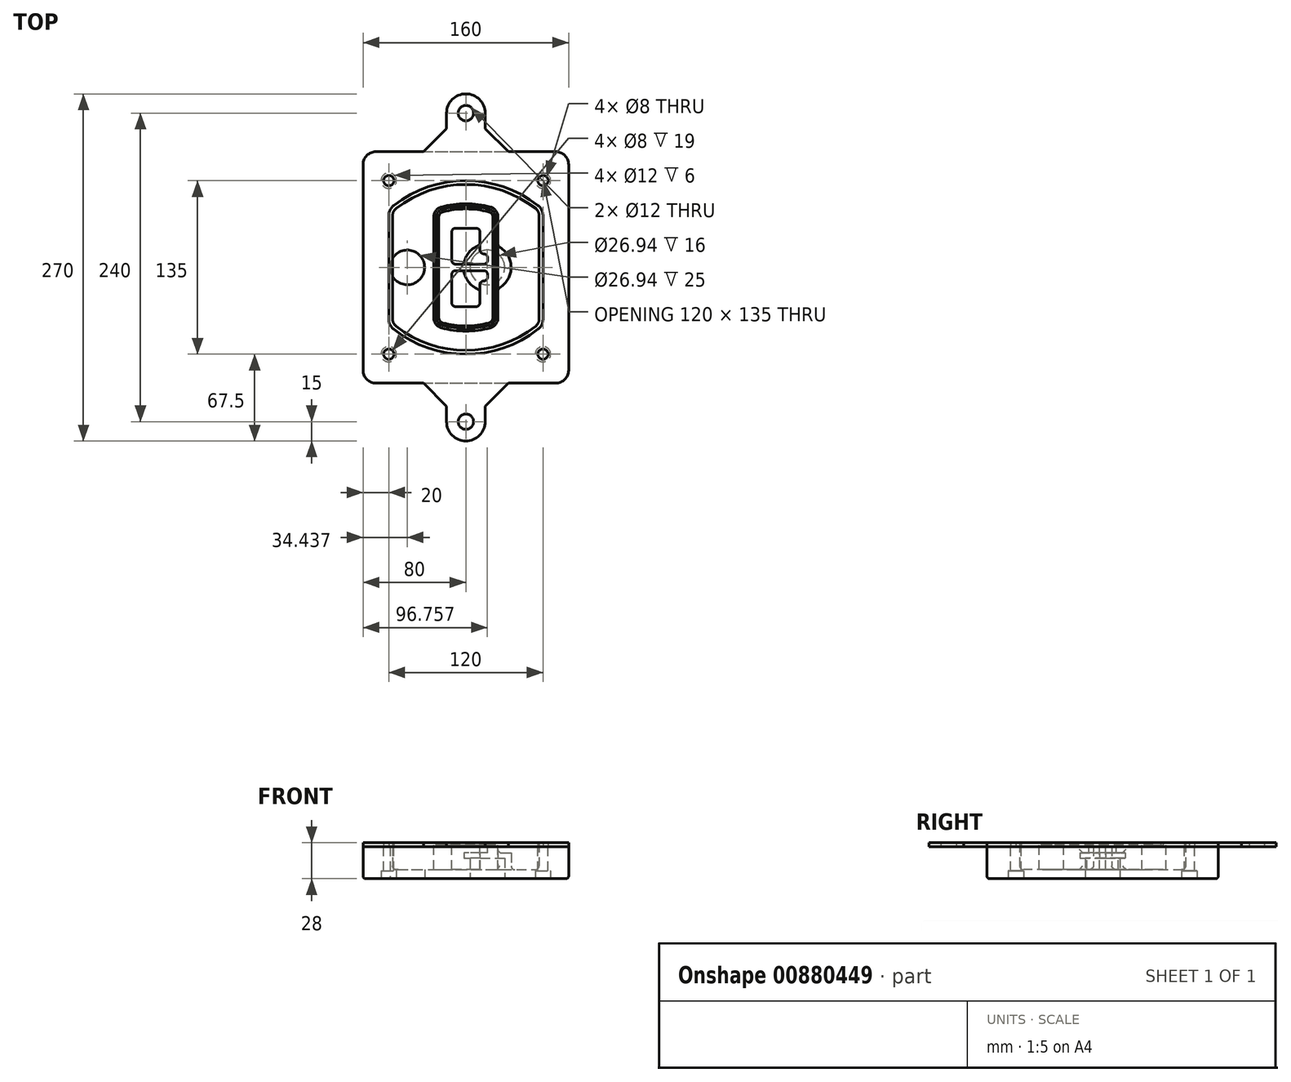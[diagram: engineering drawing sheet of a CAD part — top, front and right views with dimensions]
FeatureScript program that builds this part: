
annotation { "Feature Type Name" : "Feature", "Feature Type Description" : "" }
export const myFeature = defineFeature(function(context is Context, id is Id, definition is map)
    precondition{}
    {
        {
            var Q0;
            Q0=qCreatedBy(makeId("Top.planeOp"),FACE);
            var sketch = newSketch(context, id + "F0", { "sketchPlane" : qUnion([Q0])});
            skPoint(sketch, "E0.rect.middle", {"position": v(0, 0) * mm});
            skLineSegment(sketch, "E1.bottom", {"start": v(-70, -90) * mm, "end": v(70, -90) * mm});
            skLineSegment(sketch, "E1.top", {"start": v(-70, 90) * mm, "end": v(70, 90) * mm});
            skLineSegment(sketch, "E1.left", {"start": v(-80, -80) * mm, "end": v(-80, 80) * mm});
            skLineSegment(sketch, "E1.right", {"start": v(80, -80) * mm, "end": v(80, 80) * mm});
            skLineSegment(sketch, "E2", {"start": v(-80, 90) * mm, "end": v(80, -90) * mm, "construction": true});
            skLineSegment(sketch, "E3", {"start": v(80, 90) * mm, "end": v(-80, -90) * mm, "construction": true});
            skCircle(sketch, "E4", {"center": v(-60, 67.5) * mm, "radius": 4 * mm});
            skCircle(sketch, "E5", {"center": v(60, 67.5) * mm, "radius": 4 * mm});
            skCircle(sketch, "E6", {"center": v(60, -67.5) * mm, "radius": 4 * mm});
            skCircle(sketch, "E7", {"center": v(-60, -67.5) * mm, "radius": 4 * mm});
            skLineSegment(sketch, "E8", {"start": v(-60, 67.5) * mm, "end": v(60, 67.5) * mm, "construction": true});
            skLineSegment(sketch, "E9", {"start": v(60, 67.5) * mm, "end": v(60, -67.5) * mm, "construction": true});
            skLineSegment(sketch, "E10", {"start": v(60, -67.5) * mm, "end": v(-60, -67.5) * mm, "construction": true});
            skLineSegment(sketch, "E11", {"start": v(-60, -67.5) * mm, "end": v(-60, 67.5) * mm, "construction": true});
            skLineSegment(sketch, "E12", {"start": v(-60, 40.3) * mm, "end": v(-60, -40.3) * mm});
            skLineSegment(sketch, "E13", {"start": v(60, 40.3) * mm, "end": v(60, -40.3) * mm});
            skArc(sketch, "E14", {"start": v(56.15, 48.18) * mm, "mid": v(0, 67.5) * mm, "end": v(-56.15, 48.18) * mm});
            skArc(sketch, "E15", {"start": v(-56.15, -48.18) * mm, "mid": v(0, -67.5) * mm, "end": v(56.15, -48.18) * mm});
            skLineSegment(sketch, "E16", {"start": v(-60, 0) * mm, "end": v(60, 0) * mm, "construction": true});
            skPoint(sketch, "E17.visualSharp", {"position": v(-60, -45) * mm});
            skArc(sketch, "E17.filletArc", {"start": v(-60, -40.3) * mm, "mid": v(-58.99, -44.68) * mm, "end": v(-56.15, -48.18) * mm});
            skPoint(sketch, "E18.visualSharp", {"position": v(-60, 45) * mm});
            skArc(sketch, "E18.filletArc", {"start": v(-56.15, 48.18) * mm, "mid": v(-58.99, 44.68) * mm, "end": v(-60, 40.3) * mm});
            skPoint(sketch, "E19.visualSharp", {"position": v(60, 45) * mm});
            skArc(sketch, "E19.filletArc", {"start": v(60, 40.3) * mm, "mid": v(58.99, 44.68) * mm, "end": v(56.15, 48.18) * mm});
            skPoint(sketch, "E20.visualSharp", {"position": v(60, -45) * mm});
            skArc(sketch, "E20.filletArc", {"start": v(56.15, -48.18) * mm, "mid": v(58.99, -44.68) * mm, "end": v(60, -40.3) * mm});
            skPoint(sketch, "E21.visualSharp", {"position": v(-80, 90) * mm});
            skArc(sketch, "E21.filletArc", {"start": v(-70, 90) * mm, "mid": v(-77.07, 87.07) * mm, "end": v(-80, 80) * mm});
            skPoint(sketch, "E22.visualSharp", {"position": v(80, 90) * mm});
            skArc(sketch, "E22.filletArc", {"start": v(80, 80) * mm, "mid": v(77.07, 87.07) * mm, "end": v(70, 90) * mm});
            skPoint(sketch, "E23.visualSharp", {"position": v(80, -90) * mm});
            skArc(sketch, "E23.filletArc", {"start": v(70, -90) * mm, "mid": v(77.07, -87.07) * mm, "end": v(80, -80) * mm});
            skPoint(sketch, "E24.visualSharp", {"position": v(-80, -90) * mm});
            skArc(sketch, "E24.filletArc", {"start": v(-80, -80) * mm, "mid": v(-77.07, -87.07) * mm, "end": v(-70, -90) * mm});
            skArc(sketch, "E25.0", {"start": v(57, 40.3) * mm, "mid": v(56.3, 43.36) * mm, "end": v(54.3, 45.81) * mm});
            skLineSegment(sketch, "E25.1", {"start": v(57, 40.3) * mm, "end": v(57, -40.3) * mm});
            skArc(sketch, "E25.2", {"start": v(54.3, -45.81) * mm, "mid": v(56.3, -43.36) * mm, "end": v(57, -40.3) * mm});
            skArc(sketch, "E25.3", {"start": v(-54.3, -45.81) * mm, "mid": v(0, -64.5) * mm, "end": v(54.3, -45.81) * mm});
            skArc(sketch, "E25.4", {"start": v(-57, -40.3) * mm, "mid": v(-56.3, -43.36) * mm, "end": v(-54.3, -45.81) * mm});
            skArc(sketch, "E25.5", {"start": v(54.3, 45.81) * mm, "mid": v(0, 64.5) * mm, "end": v(-54.3, 45.81) * mm});
            skLineSegment(sketch, "E25.6", {"start": v(-57, 40.3) * mm, "end": v(-57, -40.3) * mm});
            skArc(sketch, "E25.7", {"start": v(-54.3, 45.81) * mm, "mid": v(-56.3, 43.36) * mm, "end": v(-57, 40.3) * mm});
            skArc(sketch, "E26.0", {"start": v(-58.62, 51.33) * mm, "mid": v(-62.58, 46.43) * mm, "end": v(-64, 40.3) * mm});
            skArc(sketch, "E26.1", {"start": v(58.62, 51.33) * mm, "mid": v(0, 71.5) * mm, "end": v(-58.62, 51.33) * mm});
            skArc(sketch, "E26.2", {"start": v(64, 40.3) * mm, "mid": v(62.58, 46.43) * mm, "end": v(58.62, 51.33) * mm});
            skLineSegment(sketch, "E26.3", {"start": v(64, 40.3) * mm, "end": v(64, -40.3) * mm});
            skArc(sketch, "E26.4", {"start": v(58.62, -51.33) * mm, "mid": v(62.58, -46.43) * mm, "end": v(64, -40.3) * mm});
            skLineSegment(sketch, "E26.5", {"start": v(-64, 40.3) * mm, "end": v(-64, -40.3) * mm});
            skArc(sketch, "E26.6", {"start": v(-58.62, -51.33) * mm, "mid": v(0, -71.5) * mm, "end": v(58.62, -51.33) * mm});
            skArc(sketch, "E26.7", {"start": v(-64, -40.3) * mm, "mid": v(-62.58, -46.43) * mm, "end": v(-58.62, -51.33) * mm});
            skSolve(sketch);
        }
        {
            var Q0;
            Q0=makeQuery(id+"F0.imprint","IMPRINT",FACE,{"disambiguationData":[TD([[makeQuery(id+"F0.imprint","IMPRINT",EDGE,{"derivedFrom":sQuery(id+"F0.wireOp",EDGE,"E1.bottom")}),1.0]])]});
            var Q1;
            Q1=makeQuery(id+"F0.imprint","IMPRINT",FACE,{"disambiguationData":[TD([[makeQuery(id+"F0.imprint","IMPRINT",EDGE,{"derivedFrom":sQuery(id+"F0.wireOp",EDGE,"E12")}),1.0]])]});
            var Q2;
            Q2=makeQuery(id+"F0.imprint","IMPRINT",FACE,{"disambiguationData":[TD([[makeQuery(id+"F0.imprint","IMPRINT",EDGE,{"derivedFrom":sQuery(id+"F0.wireOp",EDGE,"E25.0")}),1.0]])]});
            var Q3;
            Q3=makeQuery(id+"F0.imprint","IMPRINT",FACE,{"disambiguationData":[TD([[makeQuery(id+"F0.imprint","IMPRINT",EDGE,{"derivedFrom":sQuery(id+"F0.wireOp",EDGE,"E12")}),-1.0]])]});
            extrude(context, id + "F1", {"entities" : qUnion([Q0, Q1, Q2, Q3]), "oppositeDirection" : true, "depth" : 25 * mm});
        }
        {
            var Q0;
            Q0=makeQuery(id+"F0.imprint","IMPRINT",FACE,{"disambiguationData":[TD([[makeQuery(id+"F0.imprint","IMPRINT",EDGE,{"derivedFrom":sQuery(id+"F0.wireOp",EDGE,"E12")}),1.0]])]});
            extrude(context, id + "F2", {"entities" : qUnion([Q0]), "operationType" : NewBodyOperationType.ADD, "depth" : 3 * mm});
        }
        {
            var Q0;
            Q0=makeQuery(id+"F0.imprint","IMPRINT",FACE,{"disambiguationData":[TD([[makeQuery(id+"F0.imprint","IMPRINT",EDGE,{"derivedFrom":sQuery(id+"F0.wireOp",EDGE,"E25.0")}),1.0]])]});
            extrude(context, id + "F3", {"entities" : qUnion([Q0]), "operationType" : NewBodyOperationType.REMOVE, "oppositeDirection" : true, "depth" : 18 * mm});
        }
        {
            var Q0;
            Q0=makeQuery(id+"F2.opExtrude","CAP_FACE",FACE,{"disambiguationData":[OSD([sQuery(id+"F0.wireOp",EDGE,"E12"),sQuery(id+"F0.wireOp",EDGE,"E13"),sQuery(id+"F0.wireOp",EDGE,"E14"),sQuery(id+"F0.wireOp",EDGE,"E15"),sQuery(id+"F0.wireOp",EDGE,"E17.filletArc"),sQuery(id+"F0.wireOp",EDGE,"E18.filletArc"),sQuery(id+"F0.wireOp",EDGE,"E19.filletArc"),sQuery(id+"F0.wireOp",EDGE,"E20.filletArc"),sQuery(id+"F0.wireOp",EDGE,"E25.0"),sQuery(id+"F0.wireOp",EDGE,"E25.1"),sQuery(id+"F0.wireOp",EDGE,"E25.2"),sQuery(id+"F0.wireOp",EDGE,"E25.3"),sQuery(id+"F0.wireOp",EDGE,"E25.4"),sQuery(id+"F0.wireOp",EDGE,"E25.5"),sQuery(id+"F0.wireOp",EDGE,"E25.6"),sQuery(id+"F0.wireOp",EDGE,"E25.7")])],"isStart":false});
            var sketch = newSketch(context, id + "F4", { "sketchPlane" : qUnion([Q0])});
            skArc(sketch, "E27.0", {"start": v(-19.08, -46.97) * mm, "mid": v(0, -49.5) * mm, "end": v(19.08, -46.97) * mm});
            skArc(sketch, "E28.0", {"start": v(19.08, 46.97) * mm, "mid": v(0, 49.5) * mm, "end": v(-19.08, 46.97) * mm});
            skLineSegment(sketch, "E29", {"start": v(-25, 39.25) * mm, "end": v(-25, -39.25) * mm});
            skLineSegment(sketch, "E30", {"start": v(25, 39.25) * mm, "end": v(25, -39.25) * mm});
            skLineSegment(sketch, "E31", {"start": v(-25, 45.1) * mm, "end": v(25, 45.1) * mm, "construction": true});
            skLineSegment(sketch, "E32", {"start": v(-25, -45.1) * mm, "end": v(25, -45.1) * mm, "construction": true});
            skPoint(sketch, "E33.visualSharp", {"position": v(-25, 45.1) * mm});
            skArc(sketch, "E33.filletArc", {"start": v(-19.08, 46.97) * mm, "mid": v(-23.35, 44.11) * mm, "end": v(-25, 39.25) * mm});
            skPoint(sketch, "E34.visualSharp", {"position": v(25, 45.1) * mm});
            skArc(sketch, "E34.filletArc", {"start": v(25, 39.25) * mm, "mid": v(23.35, 44.11) * mm, "end": v(19.08, 46.97) * mm});
            skPoint(sketch, "E35.visualSharp", {"position": v(25, -45.1) * mm});
            skArc(sketch, "E35.filletArc", {"start": v(19.08, -46.97) * mm, "mid": v(23.35, -44.11) * mm, "end": v(25, -39.25) * mm});
            skPoint(sketch, "E36.visualSharp", {"position": v(-25, -45.1) * mm});
            skArc(sketch, "E36.filletArc", {"start": v(-25, -39.25) * mm, "mid": v(-23.35, -44.11) * mm, "end": v(-19.08, -46.97) * mm});
            skArc(sketch, "E37.0", {"start": v(54.3, 45.81) * mm, "mid": v(0, 64.5) * mm, "end": v(-54.3, 45.81) * mm});
            skArc(sketch, "E37.1", {"start": v(-54.3, 45.81) * mm, "mid": v(-56.3, 43.36) * mm, "end": v(-57, 40.3) * mm});
            skLineSegment(sketch, "E37.2", {"start": v(-57, 40.3) * mm, "end": v(-57, -40.3) * mm});
            skArc(sketch, "E37.3", {"start": v(-57, -40.3) * mm, "mid": v(-56.3, -43.36) * mm, "end": v(-54.3, -45.81) * mm});
            skArc(sketch, "E37.4", {"start": v(-54.3, -45.81) * mm, "mid": v(0, -64.5) * mm, "end": v(54.3, -45.81) * mm});
            skArc(sketch, "E37.5", {"start": v(54.3, -45.81) * mm, "mid": v(56.3, -43.36) * mm, "end": v(57, -40.3) * mm});
            skLineSegment(sketch, "E37.6", {"start": v(57, 40.3) * mm, "end": v(57, -40.3) * mm});
            skArc(sketch, "E37.7", {"start": v(57, 40.3) * mm, "mid": v(56.3, 43.36) * mm, "end": v(54.3, 45.81) * mm});
            skLineSegment(sketch, "E38.0", {"start": v(23, 39.25) * mm, "end": v(23, -39.25) * mm});
            skArc(sketch, "E38.1", {"start": v(18.56, -45.04) * mm, "mid": v(21.76, -42.9) * mm, "end": v(23, -39.25) * mm});
            skArc(sketch, "E38.2", {"start": v(-18.56, -45.04) * mm, "mid": v(0, -47.5) * mm, "end": v(18.56, -45.04) * mm});
            skArc(sketch, "E38.3", {"start": v(-23, -39.25) * mm, "mid": v(-21.76, -42.9) * mm, "end": v(-18.56, -45.04) * mm});
            skLineSegment(sketch, "E38.4", {"start": v(-23, 39.25) * mm, "end": v(-23, -39.25) * mm});
            skArc(sketch, "E38.5", {"start": v(23, 39.25) * mm, "mid": v(21.76, 42.9) * mm, "end": v(18.56, 45.04) * mm});
            skArc(sketch, "E38.6", {"start": v(-18.56, 45.04) * mm, "mid": v(-21.76, 42.9) * mm, "end": v(-23, 39.25) * mm});
            skArc(sketch, "E38.7", {"start": v(18.56, 45.04) * mm, "mid": v(0, 47.5) * mm, "end": v(-18.56, 45.04) * mm});
            skArc(sketch, "E39.0", {"start": v(21, 39.25) * mm, "mid": v(20.18, 41.68) * mm, "end": v(18.04, 43.1) * mm});
            skLineSegment(sketch, "E39.1", {"start": v(21, 39.25) * mm, "end": v(21, -39.25) * mm});
            skArc(sketch, "E39.2", {"start": v(18.04, -43.1) * mm, "mid": v(20.18, -41.68) * mm, "end": v(21, -39.25) * mm});
            skArc(sketch, "E39.3", {"start": v(-18.04, -43.1) * mm, "mid": v(0, -45.5) * mm, "end": v(18.04, -43.1) * mm});
            skArc(sketch, "E39.4", {"start": v(-21, -39.25) * mm, "mid": v(-20.18, -41.68) * mm, "end": v(-18.04, -43.1) * mm});
            skArc(sketch, "E39.5", {"start": v(18.04, 43.1) * mm, "mid": v(0, 45.5) * mm, "end": v(-18.04, 43.1) * mm});
            skLineSegment(sketch, "E39.6", {"start": v(-21, 39.25) * mm, "end": v(-21, -39.25) * mm});
            skArc(sketch, "E39.7", {"start": v(-18.04, 43.1) * mm, "mid": v(-20.18, 41.68) * mm, "end": v(-21, 39.25) * mm});
            skLineSegment(sketch, "E40", {"start": v(-25, 0) * mm, "end": v(25, 0) * mm, "construction": true});
            skLineSegment(sketch, "E41", {"start": v(-11, 5.5) * mm, "end": v(-11, 27.5) * mm});
            skLineSegment(sketch, "E42", {"start": v(-8, 30.5) * mm, "end": v(8, 30.5) * mm});
            skLineSegment(sketch, "E43", {"start": v(11, 27.5) * mm, "end": v(11, 13.5) * mm});
            skLineSegment(sketch, "E44", {"start": v(14, 10.5) * mm, "end": v(14, 10.5) * mm});
            skLineSegment(sketch, "E45", {"start": v(17, 7.5) * mm, "end": v(17, 5.5) * mm});
            skLineSegment(sketch, "E46", {"start": v(14, 2.5) * mm, "end": v(-8, 2.5) * mm});
            skPoint(sketch, "E47.visualSharp", {"position": v(-11, 30.5) * mm});
            skArc(sketch, "E47.filletArc", {"start": v(-8, 30.5) * mm, "mid": v(-10.12, 29.62) * mm, "end": v(-11, 27.5) * mm});
            skPoint(sketch, "E48.visualSharp", {"position": v(11, 30.5) * mm});
            skArc(sketch, "E48.filletArc", {"start": v(11, 27.5) * mm, "mid": v(10.12, 29.62) * mm, "end": v(8, 30.5) * mm});
            skPoint(sketch, "E49.visualSharp", {"position": v(11, 10.5) * mm});
            skArc(sketch, "E49.filletArc", {"start": v(11, 13.5) * mm, "mid": v(11.88, 11.38) * mm, "end": v(14, 10.5) * mm});
            skPoint(sketch, "E50.visualSharp", {"position": v(17, 10.5) * mm});
            skArc(sketch, "E50.filletArc", {"start": v(17, 7.5) * mm, "mid": v(16.12, 9.62) * mm, "end": v(14, 10.5) * mm});
            skPoint(sketch, "E51.visualSharp", {"position": v(17, 2.5) * mm});
            skArc(sketch, "E51.filletArc", {"start": v(14, 2.5) * mm, "mid": v(16.12, 3.38) * mm, "end": v(17, 5.5) * mm});
            skPoint(sketch, "E52.visualSharp", {"position": v(-11, 2.5) * mm});
            skArc(sketch, "E52.filletArc", {"start": v(-11, 5.5) * mm, "mid": v(-10.12, 3.38) * mm, "end": v(-8, 2.5) * mm});
            skLineSegment(sketch, "E53.0.MirrorCS", {"start": v(14, -2.5) * mm, "end": v(-8, -2.5) * mm});
            skArc(sketch, "E54.0.MirrorCS", {"start": v(-11, -5.5) * mm, "mid": v(-10.12, -3.38) * mm, "end": v(-8, -2.5) * mm});
            skLineSegment(sketch, "E55.0.MirrorCS", {"start": v(-11, -5.5) * mm, "end": v(-11, -27.5) * mm});
            skArc(sketch, "E56.0.MirrorCS", {"start": v(-8, -30.5) * mm, "mid": v(-10.12, -29.62) * mm, "end": v(-11, -27.5) * mm});
            skLineSegment(sketch, "E57.0.MirrorCS", {"start": v(-8, -30.5) * mm, "end": v(8, -30.5) * mm});
            skArc(sketch, "E58.0.MirrorCS", {"start": v(11, -27.5) * mm, "mid": v(10.12, -29.62) * mm, "end": v(8, -30.5) * mm});
            skLineSegment(sketch, "E59.0.MirrorCS", {"start": v(11, -27.5) * mm, "end": v(11, -13.5) * mm});
            skArc(sketch, "E60.0.MirrorCS", {"start": v(11, -13.5) * mm, "mid": v(11.88, -11.38) * mm, "end": v(14, -10.5) * mm});
            skArc(sketch, "E61.0.MirrorCS", {"start": v(17, -7.5) * mm, "mid": v(16.12, -9.62) * mm, "end": v(14, -10.5) * mm});
            skLineSegment(sketch, "E62.0.MirrorCS", {"start": v(17, -7.5) * mm, "end": v(17, -5.5) * mm});
            skArc(sketch, "E63.0.MirrorCS", {"start": v(14, -2.5) * mm, "mid": v(16.12, -3.38) * mm, "end": v(17, -5.5) * mm});
            skSolve(sketch);
        }
        {
            var Q0;
            Q0=makeQuery(id+"F4.imprint","IMPRINT",FACE,{"disambiguationData":[TD([[makeQuery(id+"F4.imprint","IMPRINT",EDGE,{"derivedFrom":sQuery(id+"F4.wireOp",EDGE,"E27.0")}),1.0]])]});
            var Q1;
            Q1=makeQuery(id+"F4.imprint","IMPRINT",FACE,{"disambiguationData":[TD([[makeQuery(id+"F4.imprint","IMPRINT",EDGE,{"derivedFrom":sQuery(id+"F4.wireOp",EDGE,"E38.0")}),-1.0]])]});
            var Q2;
            Q2=makeQuery(id+"F4.imprint","IMPRINT",FACE,{"disambiguationData":[TD([[makeQuery(id+"F4.imprint","IMPRINT",EDGE,{"derivedFrom":sQuery(id+"F4.wireOp",EDGE,"E39.0")}),1.0]])]});
            extrude(context, id + "F5", {"entities" : qUnion([Q0, Q1, Q2]), "operationType" : NewBodyOperationType.ADD, "endBound" : BoundingType.UP_TO_NEXT, "oppositeDirection" : true, "depth" : 25 * mm});
        }
        {
            var Q0;
            Q0=makeQuery(id+"F4.imprint","IMPRINT",FACE,{"disambiguationData":[TD([[makeQuery(id+"F4.imprint","IMPRINT",EDGE,{"derivedFrom":sQuery(id+"F4.wireOp",EDGE,"E38.0")}),-1.0]])]});
            extrude(context, id + "F6", {"entities" : qUnion([Q0]), "operationType" : NewBodyOperationType.REMOVE, "oppositeDirection" : true, "depth" : 2 * mm});
        }
        {
            var Q0;
            Q0=makeQuery(id+"F1.opExtrude","CAP_FACE",FACE,{"disambiguationData":[OSD([sQuery(id+"F0.wireOp",EDGE,"E1.bottom"),sQuery(id+"F0.wireOp",EDGE,"E1.top"),sQuery(id+"F0.wireOp",EDGE,"E1.left"),sQuery(id+"F0.wireOp",EDGE,"E1.right"),sQuery(id+"F0.wireOp",EDGE,"E4"),sQuery(id+"F0.wireOp",EDGE,"E5"),sQuery(id+"F0.wireOp",EDGE,"E6"),sQuery(id+"F0.wireOp",EDGE,"E7"),sQuery(id+"F0.wireOp",EDGE,"E21.filletArc"),sQuery(id+"F0.wireOp",EDGE,"E22.filletArc"),sQuery(id+"F0.wireOp",EDGE,"E23.filletArc"),sQuery(id+"F0.wireOp",EDGE,"E24.filletArc")])],"isStart":false});
            var sketch = newSketch(context, id + "F7", { "sketchPlane" : qUnion([Q0])});
            skCircle(sketch, "E64", {"center": v(16.76, 0) * mm, "radius": 13.47 * mm});
            skCircle(sketch, "E65", {"center": v(-45.56, 0) * mm, "radius": 13.47 * mm});
            skLineSegment(sketch, "E66", {"start": v(80, 0) * mm, "end": v(-80, 0) * mm});
            skCircle(sketch, "E67", {"center": v(16.76, 0) * mm, "radius": 18.47 * mm});
            skCircle(sketch, "E68", {"center": v(60, -67.5) * mm, "radius": 6 * mm});
            skCircle(sketch, "E69", {"center": v(-60, -67.5) * mm, "radius": 6 * mm});
            skCircle(sketch, "E70", {"center": v(-60, 67.5) * mm, "radius": 6 * mm});
            skCircle(sketch, "E71", {"center": v(60, 67.5) * mm, "radius": 6 * mm});
            skSolve(sketch);
        }
        {
            var Q0;
            {var subQ1=sQuery(id+"F7.wireOp",EDGE,"E66");var subQ4=sQuery(id+"F7.wireOp",EDGE,"E64");var subQ6=makeQuery(id+"F7.imprint","INTERSECT",VERTEX,{"disambiguationData":[OD(0.0)],"derivedFrom":[subQ4,subQ1]});Q0=makeQuery(id+"F7.imprint","IMPRINT",FACE,{"disambiguationData":[TD([[makeQuery(id+"F7.imprint","IMPRINT",EDGE,{"disambiguationData":[TD([[subQ6,-1.0]])],"derivedFrom":subQ4}),-1.0]])]});}
            var Q1;
            {var subQ0=sQuery(id+"F7.wireOp",EDGE,"E66");var subQ1=sQuery(id+"F7.wireOp",EDGE,"E64");var subQ3=makeQuery(id+"F7.imprint","INTERSECT",VERTEX,{"disambiguationData":[OD(0.0)],"derivedFrom":[subQ1,subQ0]});Q1=makeQuery(id+"F7.imprint","IMPRINT",FACE,{"disambiguationData":[TD([[makeQuery(id+"F7.imprint","IMPRINT",EDGE,{"disambiguationData":[TD([[subQ3,-1.0]])],"derivedFrom":subQ1}),1.0]])]});}
            var Q2;
            {var subQ0=sQuery(id+"F7.wireOp",EDGE,"E66");var subQ1=sQuery(id+"F7.wireOp",EDGE,"E64");var subQ3=makeQuery(id+"F7.imprint","INTERSECT",VERTEX,{"disambiguationData":[OD(0.0)],"derivedFrom":[subQ1,subQ0]});Q2=makeQuery(id+"F7.imprint","IMPRINT",FACE,{"disambiguationData":[TD([[makeQuery(id+"F7.imprint","IMPRINT",EDGE,{"disambiguationData":[TD([[subQ3,1.0]])],"derivedFrom":subQ1}),1.0]])]});}
            var Q3;
            {var subQ1=sQuery(id+"F7.wireOp",EDGE,"E66");var subQ4=sQuery(id+"F7.wireOp",EDGE,"E64");var subQ6=makeQuery(id+"F7.imprint","INTERSECT",VERTEX,{"disambiguationData":[OD(0.0)],"derivedFrom":[subQ4,subQ1]});Q3=makeQuery(id+"F7.imprint","IMPRINT",FACE,{"disambiguationData":[TD([[makeQuery(id+"F7.imprint","IMPRINT",EDGE,{"disambiguationData":[TD([[subQ6,1.0]])],"derivedFrom":subQ4}),-1.0]])]});}
            extrude(context, id + "F8", {"entities" : qUnion([Q0, Q1, Q2, Q3]), "operationType" : NewBodyOperationType.ADD, "oppositeDirection" : true, "depth" : 20 * mm});
        }
        {
            var Q0;
            {var subQ0=sQuery(id+"F7.wireOp",EDGE,"E66");var subQ1=sQuery(id+"F7.wireOp",EDGE,"E64");var subQ3=makeQuery(id+"F7.imprint","INTERSECT",VERTEX,{"disambiguationData":[OD(0.0)],"derivedFrom":[subQ1,subQ0]});Q0=makeQuery(id+"F7.imprint","IMPRINT",FACE,{"disambiguationData":[TD([[makeQuery(id+"F7.imprint","IMPRINT",EDGE,{"disambiguationData":[TD([[subQ3,-1.0]])],"derivedFrom":subQ1}),1.0]])]});}
            var Q1;
            {var subQ0=sQuery(id+"F7.wireOp",EDGE,"E66");var subQ1=sQuery(id+"F7.wireOp",EDGE,"E64");var subQ3=makeQuery(id+"F7.imprint","INTERSECT",VERTEX,{"disambiguationData":[OD(0.0)],"derivedFrom":[subQ1,subQ0]});Q1=makeQuery(id+"F7.imprint","IMPRINT",FACE,{"disambiguationData":[TD([[makeQuery(id+"F7.imprint","IMPRINT",EDGE,{"disambiguationData":[TD([[subQ3,1.0]])],"derivedFrom":subQ1}),1.0]])]});}
            extrude(context, id + "F9", {"entities" : qUnion([Q0, Q1]), "operationType" : NewBodyOperationType.REMOVE, "oppositeDirection" : true, "depth" : 16 * mm});
        }
        {
            var Q0;
            {var subQ0=sQuery(id+"F7.wireOp",EDGE,"E66");var subQ1=sQuery(id+"F7.wireOp",EDGE,"E65");var subQ3=makeQuery(id+"F7.imprint","INTERSECT",VERTEX,{"disambiguationData":[OD(0.0)],"derivedFrom":[subQ1,subQ0]});Q0=makeQuery(id+"F7.imprint","IMPRINT",FACE,{"disambiguationData":[TD([[makeQuery(id+"F7.imprint","IMPRINT",EDGE,{"disambiguationData":[TD([[subQ3,-1.0]])],"derivedFrom":subQ1}),1.0]])]});}
            var Q1;
            {var subQ0=sQuery(id+"F7.wireOp",EDGE,"E66");var subQ1=sQuery(id+"F7.wireOp",EDGE,"E65");var subQ3=makeQuery(id+"F7.imprint","INTERSECT",VERTEX,{"disambiguationData":[OD(0.0)],"derivedFrom":[subQ1,subQ0]});Q1=makeQuery(id+"F7.imprint","IMPRINT",FACE,{"disambiguationData":[TD([[makeQuery(id+"F7.imprint","IMPRINT",EDGE,{"disambiguationData":[TD([[subQ3,1.0]])],"derivedFrom":subQ1}),1.0]])]});}
            extrude(context, id + "F10", {"entities" : qUnion([Q0, Q1]), "operationType" : NewBodyOperationType.REMOVE, "oppositeDirection" : true, "depth" : 25 * mm});
        }
        {
            var Q0;
            Q0=makeQuery(id+"F7.imprint","IMPRINT",FACE,{"disambiguationData":[TD([[makeQuery(id+"F7.imprint","IMPRINT",EDGE,{"derivedFrom":sQuery(id+"F7.wireOp",EDGE,"E68")}),1.0]])]});
            var Q1;
            Q1=makeQuery(id+"F7.imprint","IMPRINT",FACE,{"disambiguationData":[TD([[makeQuery(id+"F7.imprint","IMPRINT",EDGE,{"derivedFrom":makeQuery(id+"F1.opExtrude","CAP_EDGE",EDGE,{"disambiguationData":[OSD([sQuery(id+"F0.wireOp",EDGE,"E5")])],"isStart":false})}),-1.0]])]});
            var Q2;
            Q2=makeQuery(id+"F7.imprint","IMPRINT",FACE,{"disambiguationData":[TD([[makeQuery(id+"F7.imprint","IMPRINT",EDGE,{"derivedFrom":sQuery(id+"F7.wireOp",EDGE,"E69")}),1.0]])]});
            var Q3;
            Q3=makeQuery(id+"F7.imprint","IMPRINT",FACE,{"disambiguationData":[TD([[makeQuery(id+"F7.imprint","IMPRINT",EDGE,{"derivedFrom":makeQuery(id+"F1.opExtrude","CAP_EDGE",EDGE,{"disambiguationData":[OSD([sQuery(id+"F0.wireOp",EDGE,"E4")])],"isStart":false})}),-1.0]])]});
            var Q4;
            Q4=makeQuery(id+"F7.imprint","IMPRINT",FACE,{"disambiguationData":[TD([[makeQuery(id+"F7.imprint","IMPRINT",EDGE,{"derivedFrom":sQuery(id+"F7.wireOp",EDGE,"E70")}),1.0]])]});
            var Q5;
            Q5=makeQuery(id+"F7.imprint","IMPRINT",FACE,{"disambiguationData":[TD([[makeQuery(id+"F7.imprint","IMPRINT",EDGE,{"derivedFrom":makeQuery(id+"F1.opExtrude","CAP_EDGE",EDGE,{"disambiguationData":[OSD([sQuery(id+"F0.wireOp",EDGE,"E7")])],"isStart":false})}),-1.0]])]});
            var Q6;
            Q6=makeQuery(id+"F7.imprint","IMPRINT",FACE,{"disambiguationData":[TD([[makeQuery(id+"F7.imprint","IMPRINT",EDGE,{"derivedFrom":sQuery(id+"F7.wireOp",EDGE,"E71")}),1.0]])]});
            var Q7;
            Q7=makeQuery(id+"F7.imprint","IMPRINT",FACE,{"disambiguationData":[TD([[makeQuery(id+"F7.imprint","IMPRINT",EDGE,{"derivedFrom":makeQuery(id+"F1.opExtrude","CAP_EDGE",EDGE,{"disambiguationData":[OSD([sQuery(id+"F0.wireOp",EDGE,"E6")])],"isStart":false})}),-1.0]])]});
            extrude(context, id + "F11", {"entities" : qUnion([Q0, Q1, Q2, Q3, Q4, Q5, Q6, Q7]), "operationType" : NewBodyOperationType.REMOVE, "oppositeDirection" : true, "depth" : 6 * mm});
        }
        {
            var Q0;
            Q0=makeQuery(id+"F9.boolean.opBoolean","COPY",FACE,{"derivedFrom":makeQuery(id+"F9.opExtrude","CAP_FACE",FACE,{"disambiguationData":[OSD([sQuery(id+"F7.wireOp",EDGE,"E64")])],"isStart":false})});
            var sketch = newSketch(context, id + "F12", { "sketchPlane" : qUnion([Q0])});
            skArc(sketch, "E72.0", {"start": v(11, 17.55) * mm, "mid": v(2.57, 11.82) * mm, "end": v(-1.54, 2.5) * mm});
            skArc(sketch, "E72.1", {"start": v(-1.54, -2.5) * mm, "mid": v(2.57, -11.82) * mm, "end": v(11, -17.55) * mm});
            skLineSegment(sketch, "E73", {"start": v(-1.54, -2.5) * mm, "end": v(14, -2.5) * mm});
            skLineSegment(sketch, "E74.0", {"start": v(14, 2.5) * mm, "end": v(-1.54, 2.5) * mm});
            skArc(sketch, "E74.1", {"start": v(14, 2.5) * mm, "mid": v(16.12, 3.38) * mm, "end": v(17, 5.5) * mm});
            skLineSegment(sketch, "E74.2", {"start": v(17, 7.5) * mm, "end": v(17, 5.5) * mm});
            skArc(sketch, "E74.3", {"start": v(17, 7.5) * mm, "mid": v(16.12, 9.62) * mm, "end": v(14, 10.5) * mm});
            skArc(sketch, "E74.4", {"start": v(11, 13.5) * mm, "mid": v(11.88, 11.38) * mm, "end": v(14, 10.5) * mm});
            skLineSegment(sketch, "E74.5", {"start": v(11, 17.55) * mm, "end": v(11, 13.5) * mm});
            skLineSegment(sketch, "E74.7", {"start": v(14, -2.5) * mm, "end": v(-1.54, -2.5) * mm});
            skArc(sketch, "E74.8", {"start": v(14, -2.5) * mm, "mid": v(16.12, -3.38) * mm, "end": v(17, -5.5) * mm});
            skLineSegment(sketch, "E74.9", {"start": v(17, -7.5) * mm, "end": v(17, -5.5) * mm});
            skArc(sketch, "E74.10", {"start": v(17, -7.5) * mm, "mid": v(16.12, -9.62) * mm, "end": v(14, -10.5) * mm});
            skArc(sketch, "E74.11", {"start": v(11, -13.5) * mm, "mid": v(11.88, -11.38) * mm, "end": v(14, -10.5) * mm});
            skLineSegment(sketch, "E74.12", {"start": v(11, -17.55) * mm, "end": v(11, -13.5) * mm});
            skPoint(sketch, "E75.orphan", {"position": v(11, -27.5) * mm});
            skPoint(sketch, "E76.orphan", {"position": v(-8, -2.5) * mm});
            skPoint(sketch, "E77.orphan", {"position": v(-8, 2.5) * mm});
            skPoint(sketch, "E78.orphan", {"position": v(11, 27.5) * mm});
            skSolve(sketch);
        }
        {
            var Q0;
            {var subQ7=sQuery(id+"F12.wireOp",EDGE,"E72.0");var subQ14=sQuery(id+"F12.wireOp",EDGE,"E72.1");var subQ16=sQuery(id+"F12.wireOp",EDGE,"E74.1");var subQ18=sQuery(id+"F12.wireOp",EDGE,"E74.8");Q0=qUnion([makeQuery(id+"F12.imprint","IMPRINT",FACE,{"disambiguationData":[TD([[makeQuery(id+"F12.imprint","IMPRINT",EDGE,{"derivedFrom":subQ7}),1.0]])]}),makeQuery(id+"F12.imprint","IMPRINT",FACE,{"disambiguationData":[TD([[makeQuery(id+"F12.imprint","IMPRINT",EDGE,{"derivedFrom":subQ14}),1.0]])]}),makeQuery(id+"F12.imprint","IMPRINT",FACE,{"disambiguationData":[TD([[makeQuery(id+"F12.imprint","IMPRINT",EDGE,{"derivedFrom":subQ16}),1.0]])]}),makeQuery(id+"F12.imprint","IMPRINT",FACE,{"disambiguationData":[TD([[makeQuery(id+"F12.imprint","IMPRINT",EDGE,{"derivedFrom":subQ18}),-1.0]])]})]);}
            var Q1;
            Q1=makeQuery(id+"F5.boolean.opBoolean","SPLIT",FACE,{"disambiguationData":[TD([makeQuery(id+"F5.opExtrude","SWEPT_FACE",FACE,{"disambiguationData":[OSD([sQuery(id+"F4.wireOp",EDGE,"E41")])]})])],"derivedFrom":makeQuery(id+"F3.boolean.opBoolean","COPY",FACE,{"derivedFrom":makeQuery(id+"F3.opExtrude","CAP_FACE",FACE,{"disambiguationData":[OSD([sQuery(id+"F0.wireOp",EDGE,"E25.0"),sQuery(id+"F0.wireOp",EDGE,"E25.1"),sQuery(id+"F0.wireOp",EDGE,"E25.2"),sQuery(id+"F0.wireOp",EDGE,"E25.3"),sQuery(id+"F0.wireOp",EDGE,"E25.4"),sQuery(id+"F0.wireOp",EDGE,"E25.5"),sQuery(id+"F0.wireOp",EDGE,"E25.6"),sQuery(id+"F0.wireOp",EDGE,"E25.7")])],"isStart":false})})});
            extrude(context, id + "F13", {"entities" : qUnion([Q0]), "operationType" : NewBodyOperationType.REMOVE, "endBound" : BoundingType.UP_TO_SURFACE, "endBoundEntityFace" : qUnion([Q1]), "depth" : 25 * mm});
        }
        {
            var Q0;
            Q0=makeQuery(id+"F3.boolean.opBoolean","COPY",EDGE,{"derivedFrom":makeQuery(id+"F3.opExtrude","CAP_EDGE",EDGE,{"disambiguationData":[OSD([sQuery(id+"F0.wireOp",EDGE,"E25.6")])],"isStart":false})});
            var Q1;
            Q1=makeQuery(id+"F8.boolean.opBoolean","INTERSECT",EDGE,{"derivedFrom":[makeQuery(id+"F5.opExtrude","SWEPT_FACE",FACE,{"disambiguationData":[OSD([sQuery(id+"F4.wireOp",EDGE,"E30")])]}),makeQuery(id+"F8.opExtrude","CAP_FACE",FACE,{"disambiguationData":[OSD([sQuery(id+"F7.wireOp",EDGE,"E67")])],"isStart":false})]});
            var Q2;
            Q2=makeQuery(id+"F8.boolean.opBoolean","INTERSECT",EDGE,{"disambiguationData":[OD(1.0)],"derivedFrom":[makeQuery(id+"F5.opExtrude","SWEPT_FACE",FACE,{"disambiguationData":[OSD([sQuery(id+"F4.wireOp",EDGE,"E30")])]}),makeQuery(id+"F8.opExtrude","SWEPT_FACE",FACE,{"disambiguationData":[OSD([sQuery(id+"F7.wireOp",EDGE,"E67")])]})]});
            var Q3;
            {var subQ0=makeQuery(id+"F3.boolean.opBoolean","COPY",FACE,{"derivedFrom":makeQuery(id+"F3.opExtrude","CAP_FACE",FACE,{"disambiguationData":[OSD([sQuery(id+"F0.wireOp",EDGE,"E25.0"),sQuery(id+"F0.wireOp",EDGE,"E25.1"),sQuery(id+"F0.wireOp",EDGE,"E25.2"),sQuery(id+"F0.wireOp",EDGE,"E25.3"),sQuery(id+"F0.wireOp",EDGE,"E25.4"),sQuery(id+"F0.wireOp",EDGE,"E25.5"),sQuery(id+"F0.wireOp",EDGE,"E25.6"),sQuery(id+"F0.wireOp",EDGE,"E25.7")])],"isStart":false})});var subQ1=sQuery(id+"F4.wireOp",EDGE,"E30");Q3=makeQuery(id+"F8.boolean.opBoolean","SPLIT",EDGE,{"disambiguationData":[TD([makeQuery(id+"F5.opExtrude","SWEPT_FACE",FACE,{"disambiguationData":[OSD([sQuery(id+"F4.wireOp",EDGE,"E35.filletArc")])]})])],"derivedFrom":makeQuery(id+"F5.opExtrude","TWEAK_EDGE",EDGE,{"derivedFrom":[subQ0,makeQuery(id+"F4.imprint","IMPRINT",EDGE,{"derivedFrom":subQ1})]})});}
            var Q4;
            {var subQ0=sQuery(id+"F0.wireOp",EDGE,"E25.0");var subQ1=sQuery(id+"F0.wireOp",EDGE,"E25.1");var subQ2=sQuery(id+"F0.wireOp",EDGE,"E25.2");var subQ3=sQuery(id+"F0.wireOp",EDGE,"E25.3");var subQ4=sQuery(id+"F0.wireOp",EDGE,"E25.4");var subQ5=sQuery(id+"F0.wireOp",EDGE,"E25.5");var subQ6=sQuery(id+"F0.wireOp",EDGE,"E25.6");var subQ7=sQuery(id+"F0.wireOp",EDGE,"E25.7");Q4=makeQuery(id+"F8.boolean.opBoolean","INTERSECT",EDGE,{"derivedFrom":[makeQuery(id+"F5.boolean.opBoolean","SPLIT",FACE,{"disambiguationData":[TD([makeQuery(id+"F2.opExtrude","SWEPT_FACE",FACE,{"disambiguationData":[OSD([subQ0])]})])],"derivedFrom":makeQuery(id+"F3.boolean.opBoolean","COPY",FACE,{"derivedFrom":makeQuery(id+"F3.opExtrude","CAP_FACE",FACE,{"disambiguationData":[OSD([subQ0,subQ1,subQ2,subQ3,subQ4,subQ5,subQ6,subQ7])],"isStart":false})})}),makeQuery(id+"F8.opExtrude","SWEPT_FACE",FACE,{"disambiguationData":[OSD([sQuery(id+"F7.wireOp",EDGE,"E67")])]})]});}
            var Q5;
            Q5=makeQuery(id+"F8.boolean.opBoolean","INTERSECT",EDGE,{"disambiguationData":[OD(0.0)],"derivedFrom":[makeQuery(id+"F5.opExtrude","SWEPT_FACE",FACE,{"disambiguationData":[OSD([sQuery(id+"F4.wireOp",EDGE,"E30")])]}),makeQuery(id+"F8.opExtrude","SWEPT_FACE",FACE,{"disambiguationData":[OSD([sQuery(id+"F7.wireOp",EDGE,"E67")])]})]});
            fillet(context, id + "F14", {"entities" : qUnion([Q0, Q1, Q2, Q3, Q4, Q5]), "radius" : 3 * mm, "tangentPropagation" : true, "allowEdgeOverflow" : false});
        }
        {
            var Q0;
            Q0=makeQuery(id+"F1.opExtrude","CAP_EDGE",EDGE,{"disambiguationData":[OSD([sQuery(id+"F0.wireOp",EDGE,"E1.bottom")])],"isStart":false});
            fillet(context, id + "F15", {"entities" : qUnion([Q0]), "radius" : 2 * mm, "tangentPropagation" : true, "allowEdgeOverflow" : false});
        }
        {
            var Q0;
            {var subQ0=sQuery(id+"F0.wireOp",EDGE,"E21.filletArc");var subQ1=sQuery(id+"F0.wireOp",EDGE,"E7");var subQ2=sQuery(id+"F0.wireOp",EDGE,"E6");var subQ3=sQuery(id+"F0.wireOp",EDGE,"E5");var subQ4=sQuery(id+"F0.wireOp",EDGE,"E4");var subQ5=sQuery(id+"F0.wireOp",EDGE,"E22.filletArc");var subQ6=sQuery(id+"F0.wireOp",EDGE,"E1.bottom");var subQ7=sQuery(id+"F0.wireOp",EDGE,"E1.right");var subQ8=sQuery(id+"F0.wireOp",EDGE,"E1.top");var subQ9=sQuery(id+"F0.wireOp",EDGE,"E1.left");var subQ10=sQuery(id+"F0.wireOp",EDGE,"E23.filletArc");var subQ11=sQuery(id+"F0.wireOp",EDGE,"E24.filletArc");Q0=makeQuery(id+"F2.boolean.opBoolean","SPLIT",FACE,{"disambiguationData":[TD([makeQuery(id+"F1.opExtrude","SWEPT_FACE",FACE,{"disambiguationData":[OSD([subQ6])]})])],"derivedFrom":makeQuery(id+"F1.opExtrude","CAP_FACE",FACE,{"disambiguationData":[OSD([subQ6,subQ8,subQ9,subQ7,subQ4,subQ3,subQ2,subQ1,subQ0,subQ5,subQ10,subQ11])],"isStart":true})});}
            var sketch = newSketch(context, id + "F16", { "sketchPlane" : qUnion([Q0])});
            skLineSegment(sketch, "E79", {"start": v(0, 90) * mm, "end": v(0, 120) * mm, "construction": true});
            skCircle(sketch, "E80", {"center": v(0, 120) * mm, "radius": 6 * mm});
            skArc(sketch, "E81", {"start": v(15, 120) * mm, "mid": v(0, 135) * mm, "end": v(-15, 120) * mm});
            skLineSegment(sketch, "E82", {"start": v(-15, 120) * mm, "end": v(-15, 108) * mm});
            skLineSegment(sketch, "E83", {"start": v(15, 120) * mm, "end": v(15, 108) * mm});
            skLineSegment(sketch, "E84", {"start": v(-15, 108) * mm, "end": v(-33, 90) * mm});
            skLineSegment(sketch, "E85", {"start": v(15, 108) * mm, "end": v(33, 90) * mm});
            skLineSegment(sketch, "E86", {"start": v(-80, 0) * mm, "end": v(80, 0) * mm, "construction": true});
            skLineSegment(sketch, "E87.MirrorCS", {"start": v(15, -108) * mm, "end": v(33, -90) * mm});
            skLineSegment(sketch, "E88.MirrorCS", {"start": v(15, -120) * mm, "end": v(15, -108) * mm});
            skArc(sketch, "E89.MirrorCS", {"start": v(15, -120) * mm, "mid": v(0, -135) * mm, "end": v(-15, -120) * mm});
            skLineSegment(sketch, "E90.MirrorCS", {"start": v(-15, -120) * mm, "end": v(-15, -108) * mm});
            skLineSegment(sketch, "E91.MirrorCS", {"start": v(-15, -108) * mm, "end": v(-33, -90) * mm});
            skCircle(sketch, "E92.MirrorC", {"center": v(0, -120) * mm, "radius": 6 * mm});
            skLineSegment(sketch, "E93.MirrorCS", {"start": v(0, -90) * mm, "end": v(0, -120) * mm, "construction": true});
            skSolve(sketch);
        }
        {
            var Q0;
            Q0=makeQuery(id+"F16.imprint","IMPRINT",FACE,{"disambiguationData":[TD([[makeQuery(id+"F16.imprint","IMPRINT",EDGE,{"derivedFrom":sQuery(id+"F16.wireOp",EDGE,"E80")}),-1.0]])]});
            var Q1;
            {var subQ0=sQuery(id+"F16.wireOp",EDGE,"E87.MirrorCS");Q1=makeQuery(id+"F16.imprint","IMPRINT",FACE,{"disambiguationData":[TD([[makeQuery(id+"F16.imprint","IMPRINT",EDGE,{"derivedFrom":subQ0}),1.0]])]});}
            var Q2;
            Q2=makeQuery(id+"F16.imprint","IMPRINT",FACE,{"disambiguationData":[TD([[makeQuery(id+"F16.imprint","IMPRINT",EDGE,{"derivedFrom":makeQuery(id+"F1.opExtrude","CAP_EDGE",EDGE,{"disambiguationData":[OSD([sQuery(id+"F0.wireOp",EDGE,"E1.left")])],"isStart":true})}),-1.0]])]});
            var Q3;
            Q3=makeQuery(id+"F2.opExtrude","CAP_FACE",FACE,{"disambiguationData":[OSD([sQuery(id+"F0.wireOp",EDGE,"E12"),sQuery(id+"F0.wireOp",EDGE,"E13"),sQuery(id+"F0.wireOp",EDGE,"E14"),sQuery(id+"F0.wireOp",EDGE,"E15"),sQuery(id+"F0.wireOp",EDGE,"E17.filletArc"),sQuery(id+"F0.wireOp",EDGE,"E18.filletArc"),sQuery(id+"F0.wireOp",EDGE,"E19.filletArc"),sQuery(id+"F0.wireOp",EDGE,"E20.filletArc"),sQuery(id+"F0.wireOp",EDGE,"E25.0"),sQuery(id+"F0.wireOp",EDGE,"E25.1"),sQuery(id+"F0.wireOp",EDGE,"E25.2"),sQuery(id+"F0.wireOp",EDGE,"E25.3"),sQuery(id+"F0.wireOp",EDGE,"E25.4"),sQuery(id+"F0.wireOp",EDGE,"E25.5"),sQuery(id+"F0.wireOp",EDGE,"E25.6"),sQuery(id+"F0.wireOp",EDGE,"E25.7")])],"isStart":false});
            extrude(context, id + "F17", {"entities" : qUnion([Q0, Q1, Q2]), "endBound" : BoundingType.UP_TO_SURFACE, "depth" : 25 * mm, "endBoundEntityFace" : qUnion([Q3]), "offsetDistance" : 25 * mm});
        }
    });
